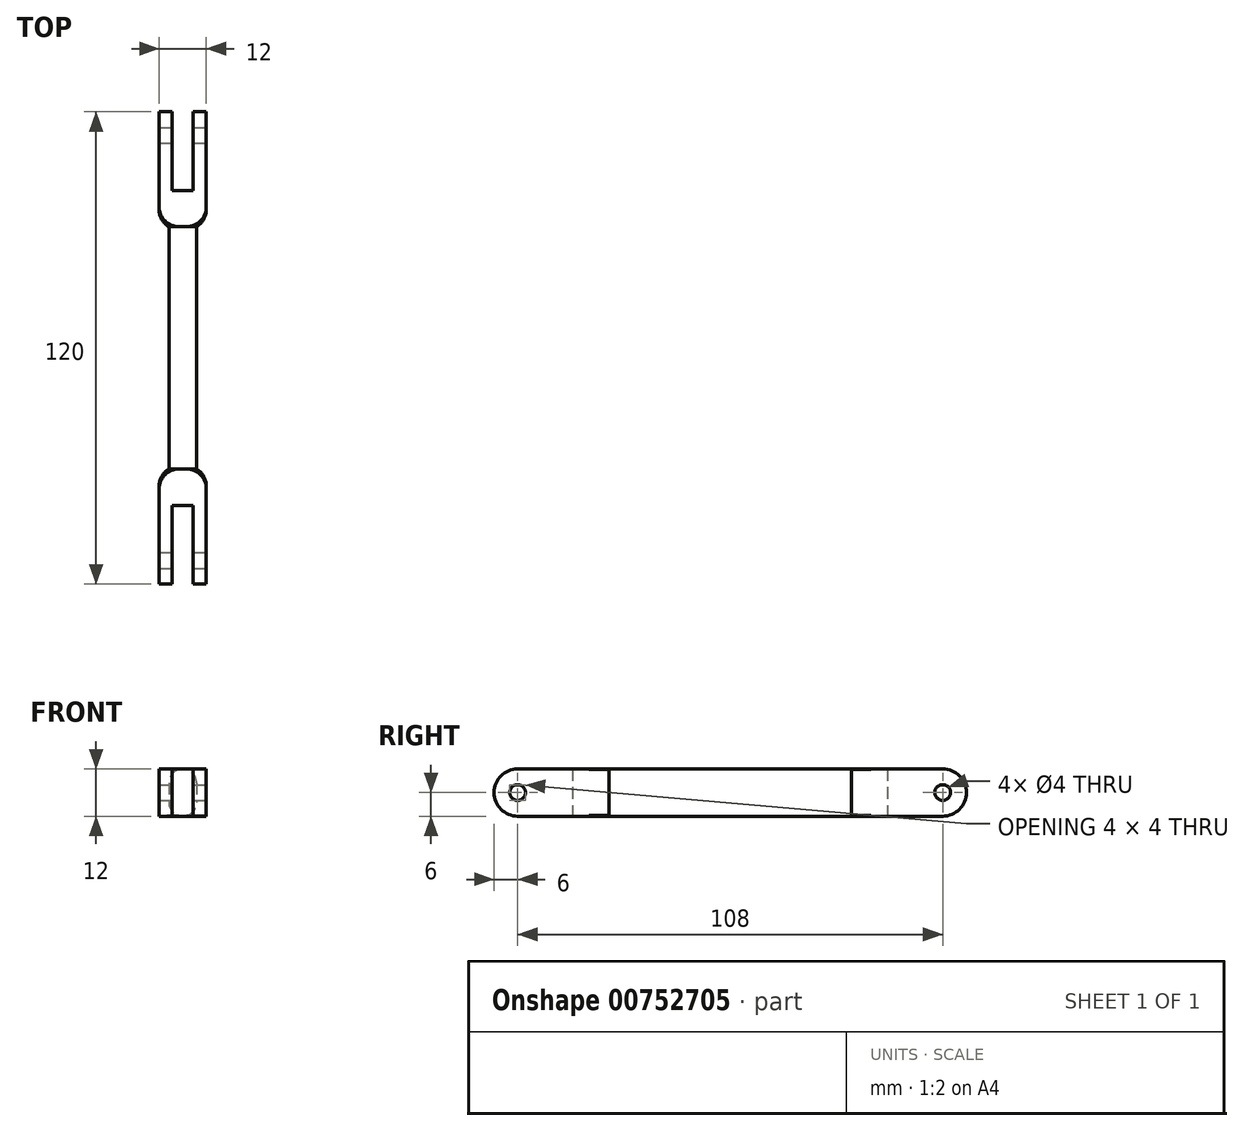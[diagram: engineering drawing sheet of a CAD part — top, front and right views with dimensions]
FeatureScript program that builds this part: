
annotation { "Feature Type Name" : "Feature", "Feature Type Description" : "" }
export const myFeature = defineFeature(function(context is Context, id is Id, definition is map)
    precondition{}
    {
        {
            var Q0;
            Q0=qCreatedBy(makeId("Top.planeOp"),FACE);
            var sketch = newSketch(context, id + "F0", { "sketchPlane" : qUnion([Q0])});
            skLineSegment(sketch, "E0.bottom", {"start": v(-6, -60) * mm, "end": v(6, -60) * mm});
            skLineSegment(sketch, "E0.top", {"start": v(-6, 60) * mm, "end": v(6, 60) * mm});
            skLineSegment(sketch, "E0.left", {"start": v(-6, -60) * mm, "end": v(-6, 60) * mm});
            skLineSegment(sketch, "E0.right", {"start": v(6, -60) * mm, "end": v(6, 60) * mm});
            skPoint(sketch, "E0.middle", {"position": v(0, 0) * mm});
            skLineSegment(sketch, "E1", {"start": v(0, -60) * mm, "end": v(0, -40) * mm, "construction": true});
            skLineSegment(sketch, "E2", {"start": v(0, -40) * mm, "end": v(2.65, -40) * mm});
            skLineSegment(sketch, "E3", {"start": v(2.65, -40) * mm, "end": v(2.65, -60) * mm});
            skLineSegment(sketch, "E4.MirrorCS", {"start": v(-2.65, -40) * mm, "end": v(-2.65, -60) * mm});
            skLineSegment(sketch, "E5.MirrorCS", {"start": v(0, -40) * mm, "end": v(-2.65, -40) * mm});
            skLineSegment(sketch, "E6", {"start": v(0, 0) * mm, "end": v(-2.66, 0) * mm, "construction": true});
            skLineSegment(sketch, "E7.MirrorCS", {"start": v(-2.65, 40) * mm, "end": v(-2.65, 60) * mm});
            skLineSegment(sketch, "E8.MirrorCS", {"start": v(2.65, 40) * mm, "end": v(2.65, 60) * mm});
            skLineSegment(sketch, "E9.MirrorCS", {"start": v(0, 40) * mm, "end": v(-2.65, 40) * mm});
            skLineSegment(sketch, "E10.MirrorCS", {"start": v(0, 40) * mm, "end": v(2.65, 40) * mm});
            skLineSegment(sketch, "E11.bottom", {"start": v(-3.5, -30.81) * mm, "end": v(3.5, -30.81) * mm});
            skLineSegment(sketch, "E11.top", {"start": v(-3.5, 30.81) * mm, "end": v(3.5, 30.81) * mm});
            skLineSegment(sketch, "E11.left", {"start": v(-3.5, -30.81) * mm, "end": v(-3.5, 30.81) * mm});
            skLineSegment(sketch, "E11.right", {"start": v(3.5, -30.81) * mm, "end": v(3.5, 30.81) * mm});
            skLineSegment(sketch, "E12", {"start": v(-3.5, -30.81) * mm, "end": v(-6, -30.81) * mm});
            skLineSegment(sketch, "E13", {"start": v(3.5, -30.81) * mm, "end": v(6, -30.81) * mm});
            skLineSegment(sketch, "E14", {"start": v(6, 30.81) * mm, "end": v(-6, 30.81) * mm});
            skSolve(sketch);
        }
        {
            var Q0;
            Q0=makeQuery(id+"F0.imprint","IMPRINT",FACE,{"disambiguationData":[TD([[makeQuery(id+"F0.imprint","IMPRINT",EDGE,{"derivedFrom":sQuery(id+"F0.wireOp",EDGE,"E11.bottom")}),1.0]])]});
            var Q1;
            {var subQ5=sQuery(id+"F0.wireOp",EDGE,"E7.MirrorCS");Q1=makeQuery(id+"F0.imprint","IMPRINT",FACE,{"disambiguationData":[TD([[makeQuery(id+"F0.imprint","IMPRINT",EDGE,{"derivedFrom":subQ5}),1.0]])]});}
            var Q2;
            Q2=makeQuery(id+"F0.imprint","IMPRINT",FACE,{"disambiguationData":[TD([[makeQuery(id+"F0.imprint","IMPRINT",EDGE,{"derivedFrom":sQuery(id+"F0.wireOp",EDGE,"E2")}),1.0]])]});
            extrude(context, id + "F1", {"entities" : qUnion([Q0, Q1, Q2]), "depth" : 12 * mm, "offsetDistance" : 25 * mm});
        }
        {
            var Q0;
            {var subQ0=sQuery(id+"F0.wireOp",EDGE,"E0.bottom");Q0=makeQuery(id+"F1.opExtrude","CAP_EDGE",EDGE,{"disambiguationData":[OSD([subQ0]),TDD([makeQuery(id+"F0.imprint","IMPRINT",EDGE,{"disambiguationData":[TD([[makeQuery(id+"F0.imprint","INTERSECT",VERTEX,{"derivedFrom":[subQ0,sQuery(id+"F0.wireOp",EDGE,"E0.right")]}),1.0]])],"derivedFrom":subQ0})])],"isStart":false});}
            var Q1;
            {var subQ0=sQuery(id+"F0.wireOp",EDGE,"E0.bottom");Q1=makeQuery(id+"F1.opExtrude","CAP_EDGE",EDGE,{"disambiguationData":[OSD([subQ0]),TDD([makeQuery(id+"F0.imprint","IMPRINT",EDGE,{"disambiguationData":[TD([[makeQuery(id+"F0.imprint","INTERSECT",VERTEX,{"derivedFrom":[subQ0,sQuery(id+"F0.wireOp",EDGE,"E0.right")]}),1.0]])],"derivedFrom":subQ0})])],"isStart":true});}
            var Q2;
            {var subQ0=sQuery(id+"F0.wireOp",EDGE,"E0.bottom");Q2=makeQuery(id+"F1.opExtrude","CAP_EDGE",EDGE,{"disambiguationData":[OSD([subQ0]),TDD([makeQuery(id+"F0.imprint","IMPRINT",EDGE,{"disambiguationData":[TD([[makeQuery(id+"F0.imprint","INTERSECT",VERTEX,{"derivedFrom":[subQ0,sQuery(id+"F0.wireOp",EDGE,"E4.MirrorCS")]}),1.0]])],"derivedFrom":subQ0})])],"isStart":false});}
            var Q3;
            {var subQ0=sQuery(id+"F0.wireOp",EDGE,"E0.bottom");Q3=makeQuery(id+"F1.opExtrude","CAP_EDGE",EDGE,{"disambiguationData":[OSD([subQ0]),TDD([makeQuery(id+"F0.imprint","IMPRINT",EDGE,{"disambiguationData":[TD([[makeQuery(id+"F0.imprint","INTERSECT",VERTEX,{"derivedFrom":[subQ0,sQuery(id+"F0.wireOp",EDGE,"E4.MirrorCS")]}),1.0]])],"derivedFrom":subQ0})])],"isStart":true});}
            var Q4;
            {var subQ0=sQuery(id+"F0.wireOp",EDGE,"E0.top");Q4=makeQuery(id+"F1.opExtrude","CAP_EDGE",EDGE,{"disambiguationData":[OSD([subQ0]),TDD([makeQuery(id+"F0.imprint","IMPRINT",EDGE,{"disambiguationData":[TD([[makeQuery(id+"F0.imprint","INTERSECT",VERTEX,{"derivedFrom":[subQ0,sQuery(id+"F0.wireOp",EDGE,"E0.right")]}),1.0]])],"derivedFrom":subQ0})])],"isStart":false});}
            var Q5;
            {var subQ0=sQuery(id+"F0.wireOp",EDGE,"E0.top");Q5=makeQuery(id+"F1.opExtrude","CAP_EDGE",EDGE,{"disambiguationData":[OSD([subQ0]),TDD([makeQuery(id+"F0.imprint","IMPRINT",EDGE,{"disambiguationData":[TD([[makeQuery(id+"F0.imprint","INTERSECT",VERTEX,{"derivedFrom":[subQ0,sQuery(id+"F0.wireOp",EDGE,"E7.MirrorCS")]}),1.0]])],"derivedFrom":subQ0})])],"isStart":false});}
            var Q6;
            {var subQ0=sQuery(id+"F0.wireOp",EDGE,"E0.top");Q6=makeQuery(id+"F1.opExtrude","CAP_EDGE",EDGE,{"disambiguationData":[OSD([subQ0]),TDD([makeQuery(id+"F0.imprint","IMPRINT",EDGE,{"disambiguationData":[TD([[makeQuery(id+"F0.imprint","INTERSECT",VERTEX,{"derivedFrom":[subQ0,sQuery(id+"F0.wireOp",EDGE,"E7.MirrorCS")]}),1.0]])],"derivedFrom":subQ0})])],"isStart":true});}
            var Q7;
            {var subQ0=sQuery(id+"F0.wireOp",EDGE,"E0.top");Q7=makeQuery(id+"F1.opExtrude","CAP_EDGE",EDGE,{"disambiguationData":[OSD([subQ0]),TDD([makeQuery(id+"F0.imprint","IMPRINT",EDGE,{"disambiguationData":[TD([[makeQuery(id+"F0.imprint","INTERSECT",VERTEX,{"derivedFrom":[subQ0,sQuery(id+"F0.wireOp",EDGE,"E0.right")]}),1.0]])],"derivedFrom":subQ0})])],"isStart":true});}
            fillet(context, id + "F2", {"entities" : qUnion([Q0, Q1, Q2, Q3, Q4, Q5, Q6, Q7]), "radius" : 6 * mm, "tangentPropagation" : true, "allowEdgeOverflow" : false});
        }
        {
            var Q0;
            Q0=makeQuery(id+"F1.opExtrude","CAP_EDGE",EDGE,{"disambiguationData":[OSD([sQuery(id+"F0.wireOp",EDGE,"E11.right")])],"isStart":false});
            var Q1;
            Q1=makeQuery(id+"F1.opExtrude","CAP_EDGE",EDGE,{"disambiguationData":[OSD([sQuery(id+"F0.wireOp",EDGE,"E11.left")])],"isStart":false});
            var Q2;
            Q2=makeQuery(id+"F1.opExtrude","CAP_EDGE",EDGE,{"disambiguationData":[OSD([sQuery(id+"F0.wireOp",EDGE,"E11.right")])],"isStart":true});
            var Q3;
            Q3=makeQuery(id+"F1.opExtrude","CAP_EDGE",EDGE,{"disambiguationData":[OSD([sQuery(id+"F0.wireOp",EDGE,"E11.left")])],"isStart":true});
            fillet(context, id + "F3", {"entities" : qUnion([Q0, Q1, Q2, Q3]), "radius" : 3.5 * mm, "tangentPropagation" : true, "allowEdgeOverflow" : false});
        }
        {
            var Q0;
            Q0=makeQuery(id+"F1.opExtrude","SWEPT_EDGE",EDGE,{"disambiguationData":[OSD([sQuery(id+"F0.wireOp",EDGE,"E0.left"),sQuery(id+"F0.wireOp",EDGE,"E14")])]});
            var Q1;
            Q1=makeQuery(id+"F1.opExtrude","SWEPT_EDGE",EDGE,{"disambiguationData":[OSD([sQuery(id+"F0.wireOp",EDGE,"E0.left"),sQuery(id+"F0.wireOp",EDGE,"E12")])]});
            var Q2;
            Q2=makeQuery(id+"F1.opExtrude","SWEPT_EDGE",EDGE,{"disambiguationData":[OSD([sQuery(id+"F0.wireOp",EDGE,"E0.right"),sQuery(id+"F0.wireOp",EDGE,"E14")])]});
            var Q3;
            Q3=makeQuery(id+"F1.opExtrude","SWEPT_EDGE",EDGE,{"disambiguationData":[OSD([sQuery(id+"F0.wireOp",EDGE,"E0.right"),sQuery(id+"F0.wireOp",EDGE,"E13")])]});
            fillet(context, id + "F4", {"entities" : qUnion([Q0, Q1, Q2, Q3]), "radius" : 5 * mm, "tangentPropagation" : true, "allowEdgeOverflow" : false});
        }
        {
            var Q0;
            Q0=qCreatedBy(makeId("Right.planeOp"),FACE);
            var sketch = newSketch(context, id + "F5", { "sketchPlane" : qUnion([Q0])});
            skLineSegment(sketch, "E15", {"start": v(0, 0) * mm, "end": v(0, 6) * mm, "construction": true});
            skLineSegment(sketch, "E16", {"start": v(0, 6) * mm, "end": v(54, 6) * mm, "construction": true});
            skCircle(sketch, "E17", {"center": v(54, 6) * mm, "radius": 2 * mm});
            skCircle(sketch, "E18.MirrorC", {"center": v(-54, 6) * mm, "radius": 2 * mm});
            skSolve(sketch);
        }
        {
            var Q0;
            Q0 = qSketchRegion(id + "F5", true);
            extrude(context, id + "F6", {"entities" : qUnion([Q0]), "operationType" : NewBodyOperationType.REMOVE, "endBound" : BoundingType.SYMMETRIC, "oppositeDirection" : true, "depth" : 25 * mm, "offsetDistance" : 25 * mm});
        }
    });
